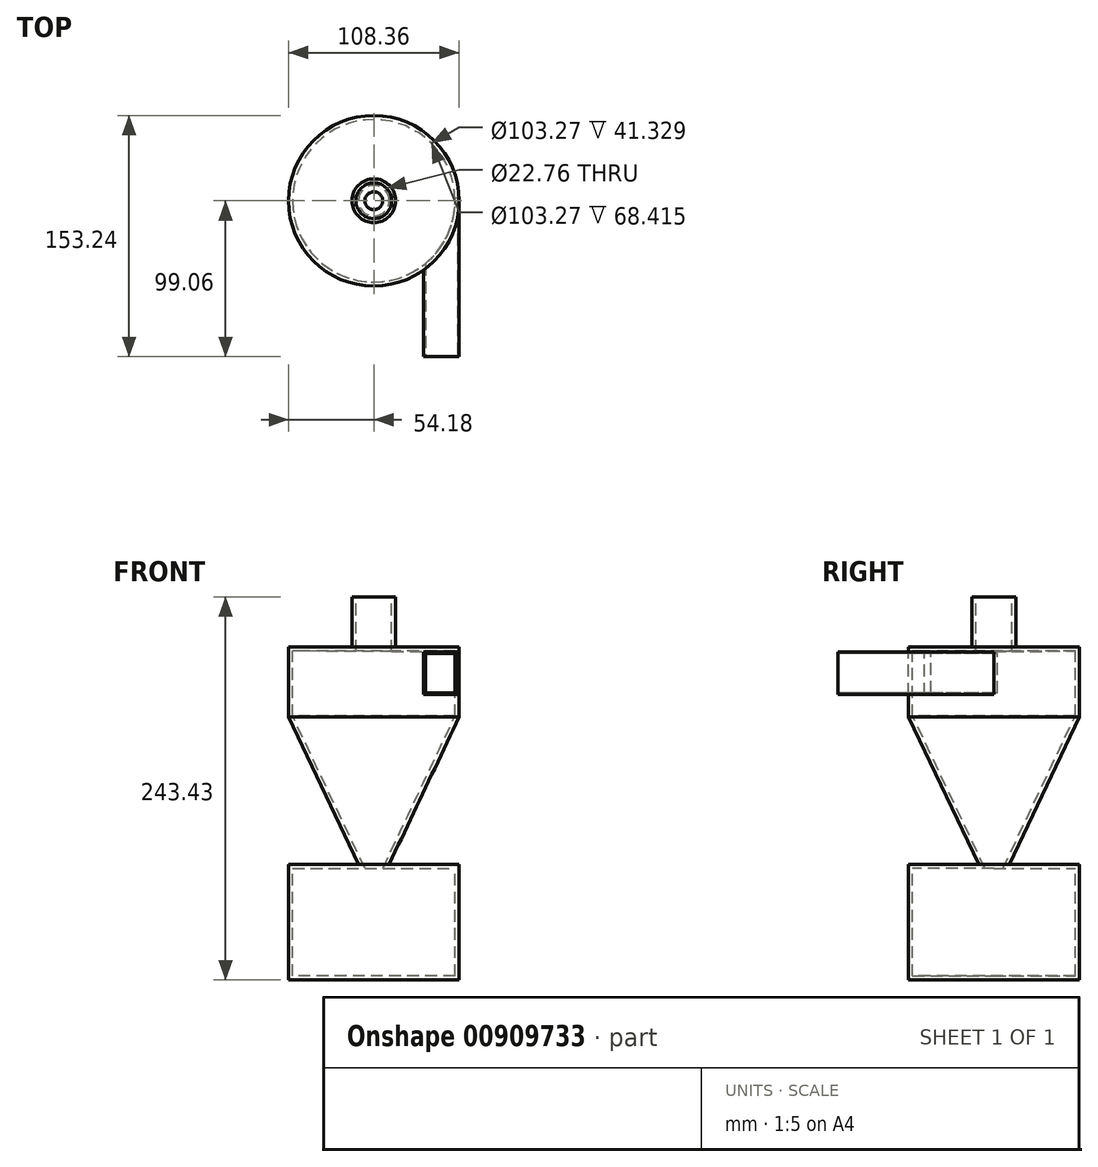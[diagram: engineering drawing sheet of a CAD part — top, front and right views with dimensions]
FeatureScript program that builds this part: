
annotation { "Feature Type Name" : "Feature", "Feature Type Description" : "" }
export const myFeature = defineFeature(function(context is Context, id is Id, definition is map)
    precondition{}
    {
        {
            var Q0;
            Q0=qCreatedBy(makeId("Front.planeOp"),FACE);
            var sketch = newSketch(context, id + "F0", { "sketchPlane" : qUnion([Q0])});
            skLineSegment(sketch, "E0", {"start": v(0, 107.5) * mm, "end": v(0, -135.92) * mm});
            skLineSegment(sketch, "E1", {"start": v(0, -135.92) * mm, "end": v(-54.18, -135.92) * mm});
            skLineSegment(sketch, "E2", {"start": v(-54.18, -135.92) * mm, "end": v(-54.18, -62.42) * mm});
            skLineSegment(sketch, "E3", {"start": v(-54.18, -62.42) * mm, "end": v(-9.7, -62.42) * mm});
            skLineSegment(sketch, "E4", {"start": v(-9.7, -62.42) * mm, "end": v(-54.18, 31.2) * mm});
            skLineSegment(sketch, "E5", {"start": v(-54.18, 31.2) * mm, "end": v(-54.18, 75.67) * mm});
            skLineSegment(sketch, "E6", {"start": v(-54.18, 75.67) * mm, "end": v(-13.92, 75.2) * mm});
            skLineSegment(sketch, "E7", {"start": v(-13.92, 75.2) * mm, "end": v(-13.92, 107.5) * mm});
            skLineSegment(sketch, "E8", {"start": v(-13.92, 107.5) * mm, "end": v(0.13, 107.04) * mm});
            skSolve(sketch);
        }
        {
            var Q0;
            Q0=qSketchRegion(id+"F0",true);
            var Q1;
            Q1=sQuery(id+"F0.wireOp",EDGE,"E0");
            revolve(context, id + "F1", {"entities" : qUnion([Q0]), "axis" : qUnion([Q1]), "revolveType" : RevolveType.FULL});
        }
        {
            var Q0;
            Q0=makeQuery(id+"F1.opRevolve","SWEPT_FACE",FACE,{"disambiguationData":[OSD([sQuery(id+"F0.wireOp",EDGE,"E8")])]});
            shell(context, id + "F2", {"entities" : qUnion([Q0]), "thickness" : 2.54 * mm});
        }
        {
            var Q0;
            Q0=qCreatedBy(makeId("Front.planeOp"),FACE);
            var sketch = newSketch(context, id + "F3", { "sketchPlane" : qUnion([Q0])});
            skLineSegment(sketch, "E9.bottom", {"start": v(54.11, 72.35) * mm, "end": v(44.53, 72.35) * mm});
            skLineSegment(sketch, "E9.top", {"start": v(54.11, 50.67) * mm, "end": v(44.53, 50.67) * mm});
            skLineSegment(sketch, "E9.left", {"start": v(54.11, 72.35) * mm, "end": v(54.11, 50.67) * mm});
            skLineSegment(sketch, "E9.right", {"start": v(44.53, 72.35) * mm, "end": v(44.53, 50.67) * mm});
            skSolve(sketch);
        }
        {
            var Q0;
            Q0=qSketchRegion(id+"F3",true);
            extrude(context, id + "F4", {"entities" : qUnion([Q0]), "operationType" : NewBodyOperationType.REMOVE, "depth" : 58.58 * mm});
        }
        {
            var Q0;
            Q0=qCreatedBy(makeId("Front.planeOp"),FACE);
            var sketch = newSketch(context, id + "F5", { "sketchPlane" : qUnion([Q0])});
            skLineSegment(sketch, "E10.bottom", {"start": v(54.18, 72.6) * mm, "end": v(31.52, 72.6) * mm});
            skLineSegment(sketch, "E10.top", {"start": v(54.18, 45.43) * mm, "end": v(31.52, 45.43) * mm});
            skLineSegment(sketch, "E10.left", {"start": v(54.18, 72.6) * mm, "end": v(54.18, 45.43) * mm});
            skLineSegment(sketch, "E10.right", {"start": v(31.52, 72.6) * mm, "end": v(31.52, 45.43) * mm});
            skSolve(sketch);
        }
        {
            var Q0;
            Q0=qSketchRegion(id+"F5",true);
            extrude(context, id + "F6", {"entities" : qUnion([Q0]), "operationType" : NewBodyOperationType.ADD, "depth" : 101.6 * mm});
        }
        {
            var Q0;
            {var subQ0=sQuery(id+"F5.wireOp",EDGE,"E10.bottom");var subQ6=sQuery(id+"F0.wireOp",EDGE,"E5");var subQ9=makeQuery(id+"F2.opShell","OFFSET_FACE",FACE,{"disambiguationData":[OSD([subQ6])]});Q0=makeQuery(id+"F6.boolean.opBoolean","SPLIT",FACE,{"disambiguationData":[TD([subQ9])],"derivedFrom":makeQuery(id+"F6.opExtrude","SWEPT_FACE",FACE,{"disambiguationData":[OSD([subQ0])]})});}
            extrude(context, id + "F7", {"entities" : qUnion([Q0]), "operationType" : NewBodyOperationType.REMOVE, "oppositeDirection" : true, "depth" : 29.38 * mm});
        }
        {
            var Q0;
            Q0=makeQuery(id+"F6.opExtrude","CAP_FACE",FACE,{"disambiguationData":[OSD([sQuery(id+"F5.wireOp",EDGE,"E10.bottom"),sQuery(id+"F5.wireOp",EDGE,"E10.top"),sQuery(id+"F5.wireOp",EDGE,"E10.left"),sQuery(id+"F5.wireOp",EDGE,"E10.right")])],"isStart":false});
            var sketch = newSketch(context, id + "F8", { "sketchPlane" : qUnion([Q0])});
            skLineSegment(sketch, "E11.bottom", {"start": v(32.68, 71.46) * mm, "end": v(53, 71.46) * mm});
            skLineSegment(sketch, "E11.top", {"start": v(32.68, 46.43) * mm, "end": v(53, 46.43) * mm});
            skLineSegment(sketch, "E11.left", {"start": v(32.68, 71.46) * mm, "end": v(32.68, 46.43) * mm});
            skLineSegment(sketch, "E11.right", {"start": v(53, 71.46) * mm, "end": v(53, 46.43) * mm});
            skSolve(sketch);
        }
        {
            var Q0;
            Q0=qSketchRegion(id+"F8",true);
            var Q1;
            Q1=makeQuery(id+"F8.imprint","IMPRINT",FACE,{"disambiguationData":[TD([[makeQuery(id+"F8.imprint","IMPRINT",EDGE,{"derivedFrom":makeQuery(id+"F6.opExtrude","CAP_EDGE",EDGE,{"disambiguationData":[OSD([sQuery(id+"F5.wireOp",EDGE,"E10.bottom")])],"isStart":false})}),1.0]])]});
            extrude(context, id + "F9", {"entities" : qUnion([Q0, Q1]), "operationType" : NewBodyOperationType.REMOVE, "oppositeDirection" : true, "depth" : 2.54 * mm});
        }
        {
            var Q0;
            Q0=qSketchRegion(id+"F8",true);
            extrude(context, id + "F10", {"entities" : qUnion([Q0]), "operationType" : NewBodyOperationType.REMOVE, "oppositeDirection" : true, "depth" : 103.65 * mm});
        }
    });
